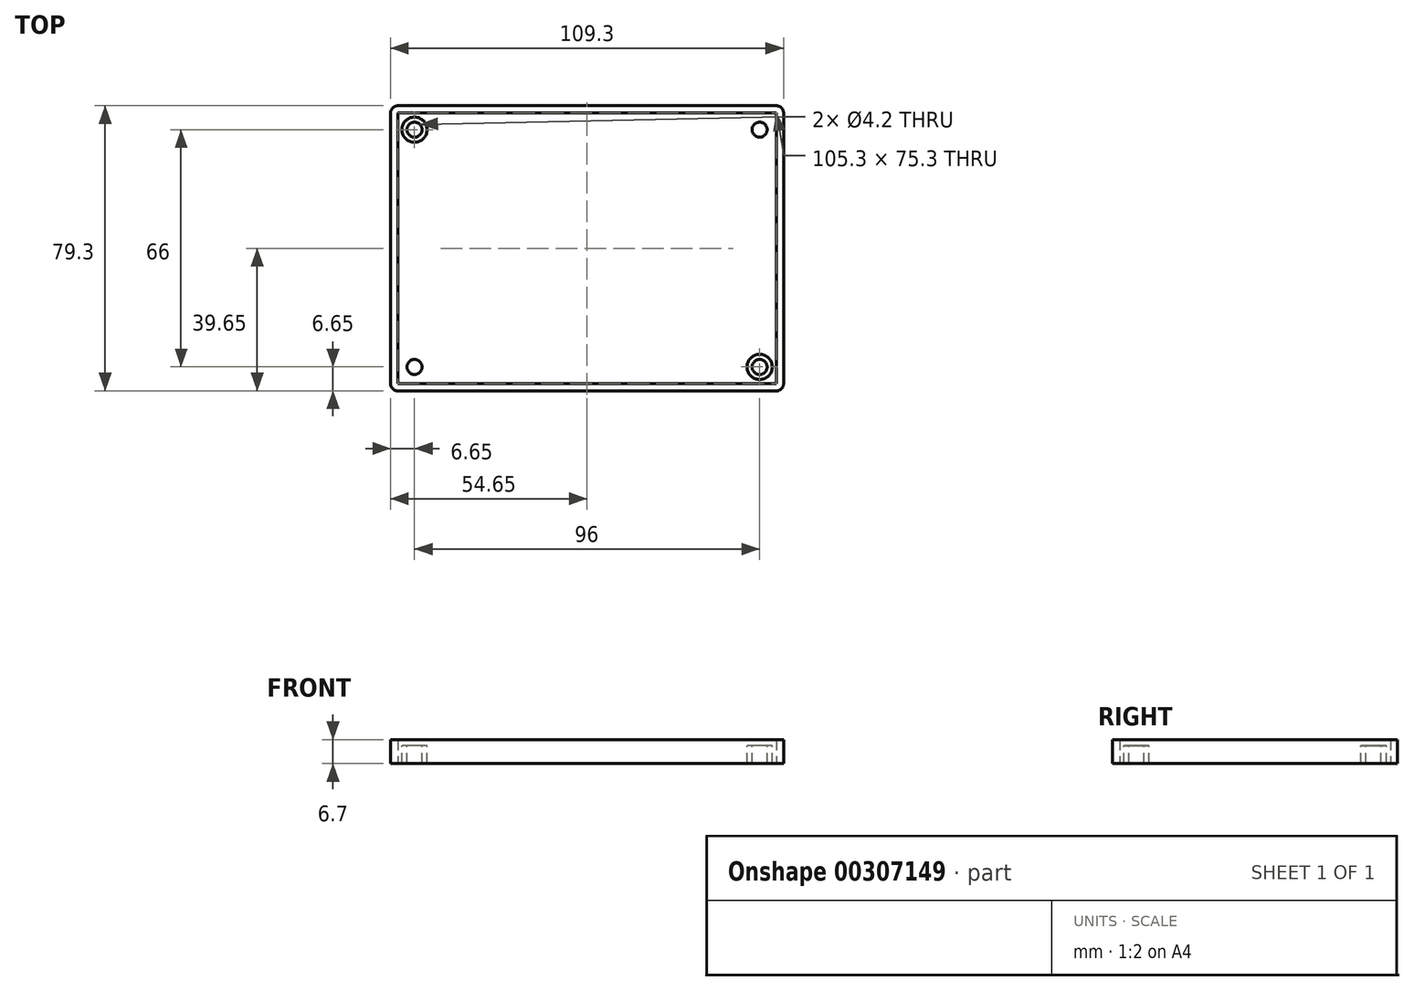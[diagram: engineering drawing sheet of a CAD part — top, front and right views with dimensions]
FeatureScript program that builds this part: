
annotation { "Feature Type Name" : "Feature", "Feature Type Description" : "" }
export const myFeature = defineFeature(function(context is Context, id is Id, definition is map)
    precondition{}
    {
        {
            var Q0;
            Q0=qCreatedBy(makeId("Top.planeOp"),FACE);
            var sketch = newSketch(context, id + "F0", { "sketchPlane" : qUnion([Q0])});
            skLineSegment(sketch, "E0.bottom", {"start": v(-52.65, 37.65) * mm, "end": v(52.65, 37.65) * mm});
            skLineSegment(sketch, "E0.top", {"start": v(-52.65, -37.65) * mm, "end": v(52.65, -37.65) * mm});
            skLineSegment(sketch, "E0.left", {"start": v(-52.65, 37.65) * mm, "end": v(-52.65, -37.65) * mm});
            skLineSegment(sketch, "E0.right", {"start": v(52.65, 37.65) * mm, "end": v(52.65, -37.65) * mm});
            skLineSegment(sketch, "E1.bottom", {"start": v(-52.65, 39.65) * mm, "end": v(52.65, 39.65) * mm});
            skLineSegment(sketch, "E1.top", {"start": v(-52.65, -39.65) * mm, "end": v(52.65, -39.65) * mm});
            skLineSegment(sketch, "E1.left", {"start": v(-54.65, 37.65) * mm, "end": v(-54.65, -37.65) * mm});
            skLineSegment(sketch, "E1.right", {"start": v(54.65, 37.65) * mm, "end": v(54.65, -37.65) * mm});
            skPoint(sketch, "E2.visualSharp", {"position": v(54.65, -39.65) * mm});
            skArc(sketch, "E2.filletArc", {"start": v(52.65, -39.65) * mm, "mid": v(54.06, -39.06) * mm, "end": v(54.65, -37.65) * mm});
            skPoint(sketch, "E3.visualSharp", {"position": v(54.65, 39.65) * mm});
            skArc(sketch, "E3.filletArc", {"start": v(54.65, 37.65) * mm, "mid": v(54.06, 39.06) * mm, "end": v(52.65, 39.65) * mm});
            skPoint(sketch, "E4.visualSharp", {"position": v(-54.65, 39.65) * mm});
            skArc(sketch, "E4.filletArc", {"start": v(-52.65, 39.65) * mm, "mid": v(-54.06, 39.06) * mm, "end": v(-54.65, 37.65) * mm});
            skPoint(sketch, "E5.visualSharp", {"position": v(-54.65, -39.65) * mm});
            skArc(sketch, "E5.filletArc", {"start": v(-54.65, -37.65) * mm, "mid": v(-54.06, -39.06) * mm, "end": v(-52.65, -39.65) * mm});
            skSolve(sketch);
        }
        {
            var Q0;
            Q0=makeQuery(id+"F0.imprint","IMPRINT",FACE,{"disambiguationData":[TD([[makeQuery(id+"F0.imprint","IMPRINT",EDGE,{"derivedFrom":sQuery(id+"F0.wireOp",EDGE,"E0.bottom")}),-1.0]])]});
            var Q1;
            Q1=makeQuery(id+"F0.imprint","IMPRINT",FACE,{"disambiguationData":[TD([[makeQuery(id+"F0.imprint","IMPRINT",EDGE,{"derivedFrom":sQuery(id+"F0.wireOp",EDGE,"E0.bottom")}),1.0]])]});
            extrude(context, id + "F1", {"entities" : qUnion([Q0, Q1]), "depth" : 2 * mm});
        }
        {
            var Q0;
            Q0=makeQuery(id+"F0.imprint","IMPRINT",FACE,{"disambiguationData":[TD([[makeQuery(id+"F0.imprint","IMPRINT",EDGE,{"derivedFrom":sQuery(id+"F0.wireOp",EDGE,"E0.bottom")}),1.0]])]});
            extrude(context, id + "F2", {"entities" : qUnion([Q0]), "operationType" : NewBodyOperationType.ADD, "depth" : 6.7 * mm});
        }
        {
            var Q0;
            Q0=makeQuery(id+"F1.opExtrude","CAP_FACE",FACE,{"disambiguationData":[OSD([sQuery(id+"F0.wireOp",EDGE,"E1.bottom"),sQuery(id+"F0.wireOp",EDGE,"E1.top"),sQuery(id+"F0.wireOp",EDGE,"E1.left"),sQuery(id+"F0.wireOp",EDGE,"E1.right"),sQuery(id+"F0.wireOp",EDGE,"E2.filletArc"),sQuery(id+"F0.wireOp",EDGE,"E3.filletArc"),sQuery(id+"F0.wireOp",EDGE,"E4.filletArc"),sQuery(id+"F0.wireOp",EDGE,"E5.filletArc")])],"isStart":false});
            var sketch = newSketch(context, id + "F3", { "sketchPlane" : qUnion([Q0])});
            skCircle(sketch, "E6", {"center": v(-48, 33) * mm, "radius": 3.5 * mm});
            skCircle(sketch, "E7", {"center": v(-48, 33) * mm, "radius": 2.1 * mm});
            skCircle(sketch, "E8.MirrorC", {"center": v(48, 33) * mm, "radius": 3.5 * mm});
            skCircle(sketch, "E9.MirrorC", {"center": v(48, 33) * mm, "radius": 2.1 * mm});
            skCircle(sketch, "E10.MirrorC", {"center": v(48, -33) * mm, "radius": 2.1 * mm});
            skCircle(sketch, "E11.MirrorC", {"center": v(-48, -33) * mm, "radius": 3.5 * mm});
            skCircle(sketch, "E12.MirrorC", {"center": v(48, -33) * mm, "radius": 3.5 * mm});
            skCircle(sketch, "E13.MirrorC", {"center": v(-48, -33) * mm, "radius": 2.1 * mm});
            skSolve(sketch);
        }
        {
            var Q0;
            Q0=makeQuery(id+"F3.imprint","IMPRINT",FACE,{"disambiguationData":[TD([[makeQuery(id+"F3.imprint","IMPRINT",EDGE,{"derivedFrom":sQuery(id+"F3.wireOp",EDGE,"E7")}),-1.0]])]});
            var Q1;
            Q1=makeQuery(id+"F3.imprint","IMPRINT",FACE,{"disambiguationData":[TD([[makeQuery(id+"F3.imprint","IMPRINT",EDGE,{"derivedFrom":sQuery(id+"F3.wireOp",EDGE,"E9.MirrorC")}),1.0]])]});
            var Q2;
            Q2=makeQuery(id+"F3.imprint","IMPRINT",FACE,{"disambiguationData":[TD([[makeQuery(id+"F3.imprint","IMPRINT",EDGE,{"derivedFrom":sQuery(id+"F3.wireOp",EDGE,"E12.MirrorC")}),1.0]])]});
            var Q3;
            Q3=makeQuery(id+"F3.imprint","IMPRINT",FACE,{"disambiguationData":[TD([[makeQuery(id+"F3.imprint","IMPRINT",EDGE,{"derivedFrom":sQuery(id+"F3.wireOp",EDGE,"E13.MirrorC")}),1.0]])]});
            extrude(context, id + "F4", {"entities" : qUnion([Q0, Q1, Q2, Q3]), "operationType" : NewBodyOperationType.ADD, "depth" : 3 * mm});
        }
        {
            var Q0;
            Q0=makeQuery(id+"F4.boolean.opBoolean","SPLIT",FACE,{"disambiguationData":[TD([makeQuery(id+"F4.opExtrude","SWEPT_FACE",FACE,{"disambiguationData":[OSD([sQuery(id+"F3.wireOp",EDGE,"E7")])]})])],"derivedFrom":makeQuery(id+"F1.opExtrude","CAP_FACE",FACE,{"disambiguationData":[OSD([sQuery(id+"F0.wireOp",EDGE,"E1.bottom"),sQuery(id+"F0.wireOp",EDGE,"E1.top"),sQuery(id+"F0.wireOp",EDGE,"E1.left"),sQuery(id+"F0.wireOp",EDGE,"E1.right"),sQuery(id+"F0.wireOp",EDGE,"E2.filletArc"),sQuery(id+"F0.wireOp",EDGE,"E3.filletArc"),sQuery(id+"F0.wireOp",EDGE,"E4.filletArc"),sQuery(id+"F0.wireOp",EDGE,"E5.filletArc")])],"isStart":false})});
            var Q1;
            Q1=makeQuery(id+"F4.boolean.opBoolean","SPLIT",FACE,{"disambiguationData":[TD([makeQuery(id+"F4.opExtrude","SWEPT_FACE",FACE,{"disambiguationData":[OSD([sQuery(id+"F3.wireOp",EDGE,"E9.MirrorC")])]})])],"derivedFrom":makeQuery(id+"F1.opExtrude","CAP_FACE",FACE,{"disambiguationData":[OSD([sQuery(id+"F0.wireOp",EDGE,"E1.bottom"),sQuery(id+"F0.wireOp",EDGE,"E1.top"),sQuery(id+"F0.wireOp",EDGE,"E1.left"),sQuery(id+"F0.wireOp",EDGE,"E1.right"),sQuery(id+"F0.wireOp",EDGE,"E2.filletArc"),sQuery(id+"F0.wireOp",EDGE,"E3.filletArc"),sQuery(id+"F0.wireOp",EDGE,"E4.filletArc"),sQuery(id+"F0.wireOp",EDGE,"E5.filletArc")])],"isStart":false})});
            var Q2;
            Q2=makeQuery(id+"F4.boolean.opBoolean","SPLIT",FACE,{"disambiguationData":[TD([makeQuery(id+"F4.opExtrude","SWEPT_FACE",FACE,{"disambiguationData":[OSD([sQuery(id+"F3.wireOp",EDGE,"E10.MirrorC")])]})])],"derivedFrom":makeQuery(id+"F1.opExtrude","CAP_FACE",FACE,{"disambiguationData":[OSD([sQuery(id+"F0.wireOp",EDGE,"E1.bottom"),sQuery(id+"F0.wireOp",EDGE,"E1.top"),sQuery(id+"F0.wireOp",EDGE,"E1.left"),sQuery(id+"F0.wireOp",EDGE,"E1.right"),sQuery(id+"F0.wireOp",EDGE,"E2.filletArc"),sQuery(id+"F0.wireOp",EDGE,"E3.filletArc"),sQuery(id+"F0.wireOp",EDGE,"E4.filletArc"),sQuery(id+"F0.wireOp",EDGE,"E5.filletArc")])],"isStart":false})});
            var Q3;
            Q3=makeQuery(id+"F4.boolean.opBoolean","SPLIT",FACE,{"disambiguationData":[TD([makeQuery(id+"F4.opExtrude","SWEPT_FACE",FACE,{"disambiguationData":[OSD([sQuery(id+"F3.wireOp",EDGE,"E13.MirrorC")])]})])],"derivedFrom":makeQuery(id+"F1.opExtrude","CAP_FACE",FACE,{"disambiguationData":[OSD([sQuery(id+"F0.wireOp",EDGE,"E1.bottom"),sQuery(id+"F0.wireOp",EDGE,"E1.top"),sQuery(id+"F0.wireOp",EDGE,"E1.left"),sQuery(id+"F0.wireOp",EDGE,"E1.right"),sQuery(id+"F0.wireOp",EDGE,"E2.filletArc"),sQuery(id+"F0.wireOp",EDGE,"E3.filletArc"),sQuery(id+"F0.wireOp",EDGE,"E4.filletArc"),sQuery(id+"F0.wireOp",EDGE,"E5.filletArc")])],"isStart":false})});
            extrude(context, id + "F5", {"entities" : qUnion([Q0, Q1, Q2, Q3]), "operationType" : NewBodyOperationType.REMOVE, "oppositeDirection" : true, "depth" : 25 * mm});
        }
    });
